# Revit family: FU_Table_Sandler_Campus Cafe Table
name_source: partatom
category: Furniture
units: mm (PartAtom-declared; Revit-internal decimal feet)

## family parameters
Always vertical = Yes
Cut with Voids When Loaded = No
OmniClass Number = 23.40.20.00
OmniClass Title = General Furniture and Specialties
Room Calculation Point = No
Shared = No
Work Plane-Based = No

## types (1)
- Campus Cafe Table Melamine 70cm (27.5")
    Assembly Code = E2020
    Default Elevation = 0 mm  [stored 0 ft]
    Description = Texture powder coated pillar frame with cast footplate. White Grey Melamine or Graphite Melamine Table Top
    Frame Material = Metal - Black - Matte
    Keynote = 46.B
    Manufacturer = Sandler
    Model = CAMPUS TABLE
    Table Top Diameter = 700 mm  [stored 2.29659 ft]
    Table Top Height = 720 mm  [stored 2.3622 ft]
    Table Top Material = Melamine - NCS S8000-N Graphite
    URL = https://www.sandlerseating.com

note: [stored X ft] marks values corroborated as IEEE doubles in the binary element streams (Revit-internal decimal feet)

## geometry (parser evidence)
native form markers: Blend x4, Sweep x2
no freeform markers — native parametric forms only
